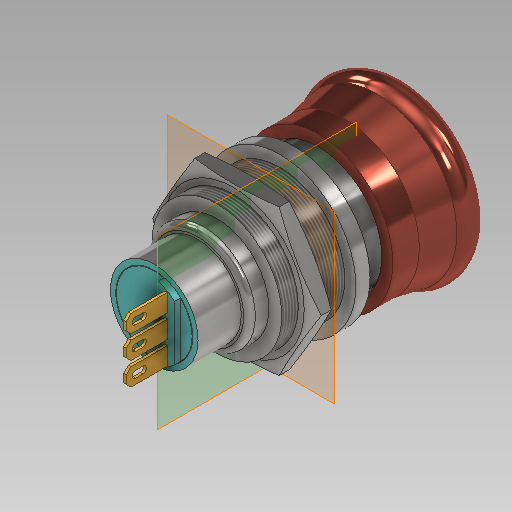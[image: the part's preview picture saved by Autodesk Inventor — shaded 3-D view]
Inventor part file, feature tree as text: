
AUTODESK INVENTOR PART (.ipt)
format: ipt  version: 2020 (Build 240168000, 168)  size: 505,856 bytes
history: native  units: mm
features: sketch x13, extrude x11, plane x2, revolve x2, chamfer x1, thread x1, fillet x1, pattern_circular x1
ambient origin geometry x8: Origin, YZ Plane, XZ Plane, XY Plane, X Axis, Y Axis, Z Axis, Center Point
bodies: Solid1 (feature_tree), Solid2 (feature_tree), Solid3 (feature_tree), Solid4 (feature_tree), Solid5 (feature_tree)
feature tree (32):
  extrude  "Extrusion1"  Depth=2.4mm TaperAngle=0.0deg
  extrude  "Extrusion2"  Depth=6.0mm TaperAngle=0.0deg
  extrude  "Extrusion3"  Depth=10.7mm TaperAngle=0.0deg
  extrude  "Extrusion4"  Depth=3.3mm TaperAngle=0.0deg
  extrude  "Extrusion5"  Depth=7.34mm TaperAngle=0.0deg
  extrude  "Extrusion6"  Depth=2.8mm
  extrude  "Extrusion7"  Depth=1.0mm
  plane  "Work Plane1"
  extrude  "Extrusion8"  Depth=1.0mm
  chamfer  "Chamfer1"  Distance=0.8mm
  revolve  "Revolution1"  [1 undecoded]
  thread  "Thread1"  [1 undecoded]
  fillet  "Fillet1"  Radius=29.0mm
  extrude  "Extrusion9"  Depth=1.0mm
  extrude  "Extrusion10"  Depth=1.0mm
  pattern_circular  "Circular Pattern1"  [2 undecoded]
  plane  "Work Plane2"
  extrude  "Extrusion11"  Depth=1.0mm
  revolve  "Revolution2"  [1 undecoded]
  sketch  "Sketch1"  dims[d0=25.78mm d1=2.4mm d2=0.0mm]
  sketch  "Sketch2"  dims[d3=20.57mm d4=6.0mm d5=0.0mm]
  sketch  "Sketch3"  dims[d6=22.0mm d7=10.7mm d8=0.0mm]
  sketch  "Sketch4"  dims[d9=17.63mm d10=3.3mm d11=0.0mm]
  sketch  "Sketch5"  dims[d12=14.85mm d13=7.34mm d14=0.0mm]
  sketch  "Sketch6"  dims[d15=5.8mm d16=2.8mm]
  sketch  "Sketch7"  dims[d17=1.0mm d18=0.0mm d19=1.0mm]
  sketch  "Sketch8"  dims[d20=1.0mm d21=0.0mm d22=3.0mm]
  sketch  "Sketch10"  dims[d23=7.0mm]
  sketch  "Sketch11"  dims[d25=4.8mm]
  sketch  "Sketch12"  dims[d26=1.16mm]
  sketch  "Sketch13"  dims[d27=2.4mm]
  sketch  "Sketch14"  dims[d28=0.8mm d29=0.8mm d30=0.45mm d31=0.0mm d32=0.8mm d33=2.0mm d34=45.0deg d35=29.0mm d36=4.1mm d37=14.7mm d38=4.5mm d39=25.3mm d40=23.3mm d41=13.67mm d42=0.5mm d43=90.0deg d44=10.7mm d45=0.0mm d46=1.0mm d47=1.0mm d48=0.1mm d49=1.0mm d50=0.0mm d51=1.5mm d52=16.0mm d53=120.0deg d54=120.0deg d55=30.0deg d56=30.0deg d57=3.0mm d58=1.5mm d59=2.0mm d60=0.75mm d61=0.001mm d62=0.0mm d63=30.0mm d64=360.0deg d66=5.0mm d67=24.8mm d68=2.9mm d69=0.0mm d70=0.8mm d71=0.8mm d72=3.0mm d73=3.0mm d74=1.0mm d75=90.0deg]
note: 5 required parameter values undecoded (feature->parameter linkage not recoverable at this tier; creation-order binding heuristic only, values carry confidence <= 0.55)